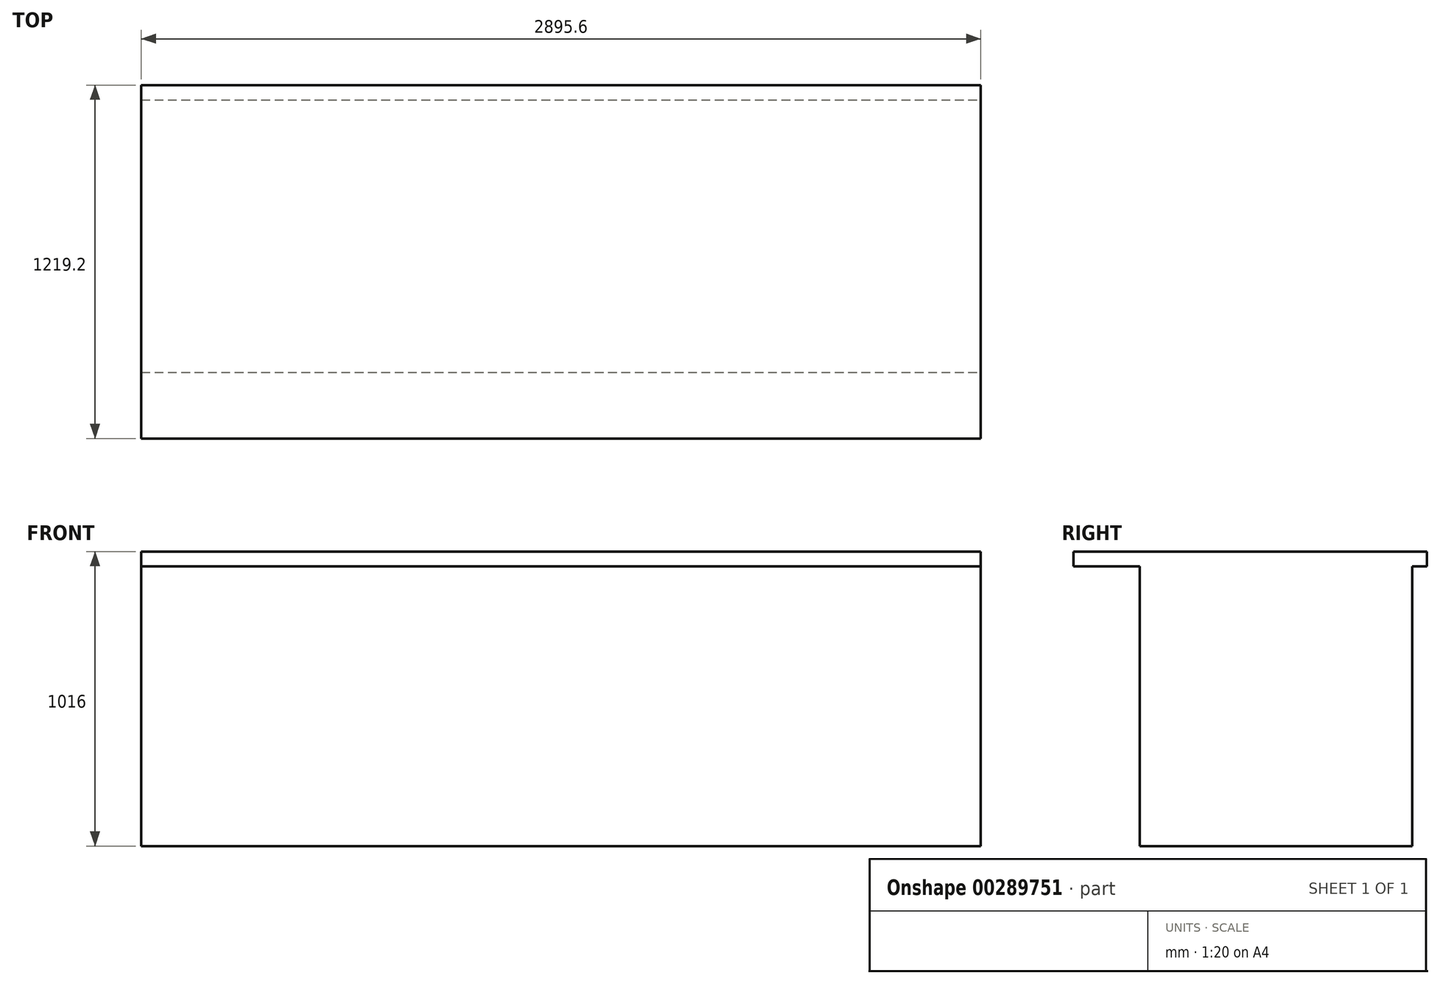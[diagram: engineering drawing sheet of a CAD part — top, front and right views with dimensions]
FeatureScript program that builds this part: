
annotation { "Feature Type Name" : "Feature", "Feature Type Description" : "" }
export const myFeature = defineFeature(function(context is Context, id is Id, definition is map)
    precondition{}
    {
        {
            var Q0;
            Q0=qCreatedBy(makeId("Top.planeOp"),FACE);
            var sketch = newSketch(context, id + "F0", { "sketchPlane" : qUnion([Q0])});
            skLineSegment(sketch, "E0.bottom", {"start": v(1447.8, -609.6) * mm, "end": v(-1447.8, -609.6) * mm});
            skLineSegment(sketch, "E0.top", {"start": v(1447.8, 609.6) * mm, "end": v(-1447.8, 609.6) * mm});
            skLineSegment(sketch, "E0.left", {"start": v(1447.8, -609.6) * mm, "end": v(1447.8, 609.6) * mm});
            skLineSegment(sketch, "E0.right", {"start": v(-1447.8, -609.6) * mm, "end": v(-1447.8, 609.6) * mm});
            skPoint(sketch, "E0.middle", {"position": v(0, 0) * mm});
            skSolve(sketch);
        }
        {
            var Q0;
            Q0=makeQuery(id+"F0.imprint","IMPRINT",FACE,{"disambiguationData":[TD([[makeQuery(id+"F0.imprint","IMPRINT",EDGE,{"derivedFrom":sQuery(id+"F0.wireOp",EDGE,"E0.bottom")}),-1.0]])]});
            extrude(context, id + "F1", {"entities" : qUnion([Q0]), "depth" : 1016 * mm, "offsetDistance" : 30.48 * mm});
        }
        {
            var Q0;
            Q0=makeQuery(id+"F1.opExtrude","SWEPT_FACE",FACE,{"disambiguationData":[OSD([sQuery(id+"F0.wireOp",EDGE,"E0.left")])]});
            var sketch = newSketch(context, id + "F2", { "sketchPlane" : qUnion([Q0])});
            skLineSegment(sketch, "E1", {"start": v(-609.6, 965.2) * mm, "end": v(-381, 965.2) * mm});
            skLineSegment(sketch, "E2", {"start": v(-381, 965.2) * mm, "end": v(-381, 0) * mm});
            skLineSegment(sketch, "E3", {"start": v(609.6, 965.2) * mm, "end": v(558.8, 965.2) * mm});
            skLineSegment(sketch, "E4", {"start": v(558.8, 965.2) * mm, "end": v(558.8, 0) * mm});
            skSolve(sketch);
        }
        {
            var Q0;
            {var subQ0=sQuery(id+"F2.wireOp",EDGE,"E1");Q0=makeQuery(id+"F2.imprint","IMPRINT",FACE,{"disambiguationData":[TD([[makeQuery(id+"F2.imprint","IMPRINT",EDGE,{"derivedFrom":subQ0}),-1.0]])]});}
            var Q1;
            {var subQ0=sQuery(id+"F2.wireOp",EDGE,"E3");Q1=makeQuery(id+"F2.imprint","IMPRINT",FACE,{"disambiguationData":[TD([[makeQuery(id+"F2.imprint","IMPRINT",EDGE,{"derivedFrom":subQ0}),1.0]])]});}
            extrude(context, id + "F3", {"entities" : qUnion([Q0, Q1]), "operationType" : NewBodyOperationType.REMOVE, "oppositeDirection" : true, "depth" : 3048 * mm, "offsetDistance" : 30.48 * mm});
        }
    });
